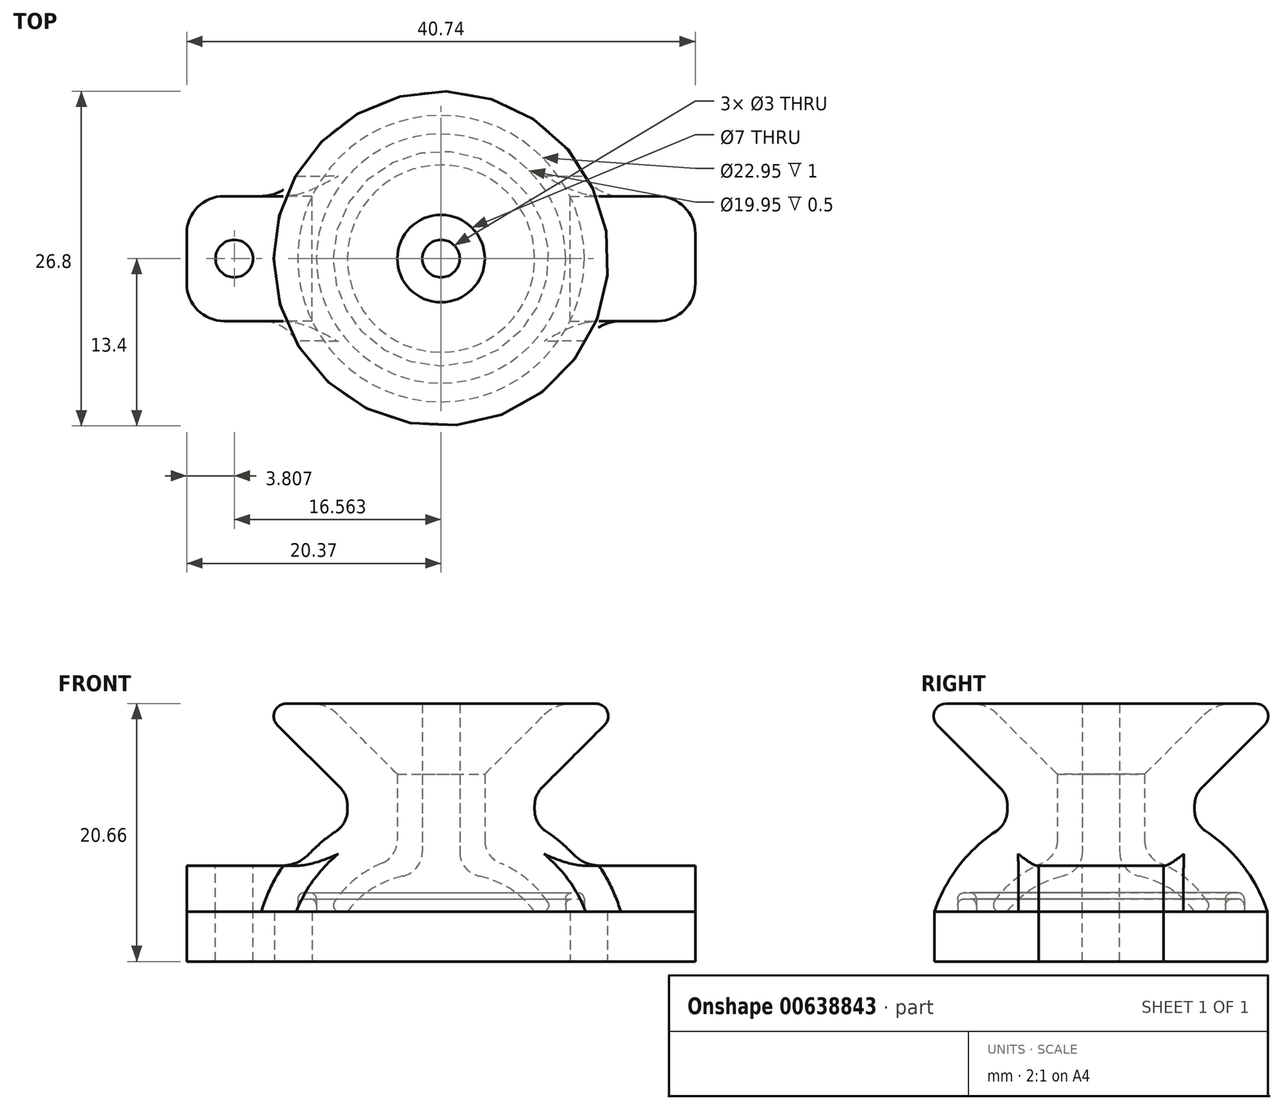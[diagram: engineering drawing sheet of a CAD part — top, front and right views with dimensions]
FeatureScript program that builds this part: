
annotation { "Feature Type Name" : "Feature", "Feature Type Description" : "" }
export const myFeature = defineFeature(function(context is Context, id is Id, definition is map)
    precondition{}
    {
        {
            var Q0;
            Q0=qCreatedBy(makeId("Front.planeOp"),FACE);
            var sketch = newSketch(context, id + "F0", { "sketchPlane" : qUnion([Q0])});
            skLineSegment(sketch, "E0", {"start": v(0, 0) * mm, "end": v(-1.5, 0) * mm, "construction": true});
            skLineSegment(sketch, "E1", {"start": v(-1.5, 1.79) * mm, "end": v(-1.5, 8) * mm});
            skPoint(sketch, "E2.endSnap0", {"position": v(-0.75, 0) * mm});
            skLineSegment(sketch, "E3", {"start": v(-1.5, 0) * mm, "end": v(-1.5, -3) * mm, "construction": true});
            skLineSegment(sketch, "E4", {"start": v(0, -3) * mm, "end": v(-7.5, -3) * mm, "construction": true});
            skLineSegment(sketch, "E5", {"start": v(-7.5, -3) * mm, "end": v(-8.12, -3) * mm});
            skArc(sketch, "E6", {"start": v(-3.08, -0.17) * mm, "mid": v(-5.55, -1.18) * mm, "end": v(-7.5, -3) * mm});
            skArc(sketch, "E7", {"start": v(-4.74, 0.87) * mm, "mid": v(-6.86, -0.4) * mm, "end": v(-8.53, -2.22) * mm});
            skLineSegment(sketch, "E8", {"start": v(-1.5, 8) * mm, "end": v(-3.5, 8) * mm});
            skLineSegment(sketch, "E9", {"start": v(-3.5, 8) * mm, "end": v(-3.5, 2.72) * mm});
            skLineSegment(sketch, "E10", {"start": v(0, -3) * mm, "end": v(0, 8.98) * mm, "construction": true});
            skPoint(sketch, "E11.visualSharp", {"position": v(-9, -3) * mm});
            skArc(sketch, "E11.filletArc", {"start": v(-8.53, -2.22) * mm, "mid": v(-8.56, -2.73) * mm, "end": v(-8.12, -3) * mm});
            skPoint(sketch, "E12.visualSharp", {"position": v(-1.5, 0) * mm});
            skArc(sketch, "E12.filletArc", {"start": v(-3.08, -0.17) * mm, "mid": v(-1.94, 0.53) * mm, "end": v(-1.5, 1.79) * mm});
            skPoint(sketch, "E13.visualSharp", {"position": v(-3.5, 1.27) * mm});
            skArc(sketch, "E13.filletArc", {"start": v(-4.74, 0.87) * mm, "mid": v(-3.84, 1.6) * mm, "end": v(-3.5, 2.72) * mm});
            skSolve(sketch);
        }
        {
            var Q0;
            Q0=makeQuery(id+"F0.imprint","IMPRINT",FACE,{"disambiguationData":[TD([[makeQuery(id+"F0.imprint","IMPRINT",EDGE,{"derivedFrom":sQuery(id+"F0.wireOp",EDGE,"E1")}),1.0]])]});
            var Q1;
            Q1=sQuery(id+"F0.wireOp",EDGE,"E10");
            revolve(context, id + "F1", {"entities" : qUnion([Q0]), "axis" : qUnion([Q1]), "revolveType" : RevolveType.FULL});
        }
        {
            var Q0;
            Q0=qCreatedBy(makeId("Front.planeOp"),FACE);
            var sketch = newSketch(context, id + "F2", { "sketchPlane" : qUnion([Q0])});
            skLineSegment(sketch, "E14.0", {"start": v(-3.5, 8) * mm, "end": v(-3.5, 2.72) * mm});
            skArc(sketch, "E14.1", {"start": v(-4.74, 0.87) * mm, "mid": v(-6.86, -0.4) * mm, "end": v(-8.53, -2.22) * mm});
            skArc(sketch, "E15.0", {"start": v(-8.4, 3.44) * mm, "mid": v(-11.4, 0.63) * mm, "end": v(-13.34, -3) * mm});
            skLineSegment(sketch, "E15.1", {"start": v(-7.5, 5.51) * mm, "end": v(-7.5, 5.1) * mm});
            skLineSegment(sketch, "E16.0", {"start": v(-1.5, 1.79) * mm, "end": v(-1.5, 8) * mm});
            skArc(sketch, "E16.1", {"start": v(-3.08, -0.17) * mm, "mid": v(-5.55, -1.18) * mm, "end": v(-7.5, -3) * mm});
            skLineSegment(sketch, "E16.2", {"start": v(-7.5, -3) * mm, "end": v(-8.12, -3) * mm});
            skArc(sketch, "E17.0", {"start": v(-4.74, 0.87) * mm, "mid": v(-3.84, 1.6) * mm, "end": v(-3.5, 2.72) * mm});
            skArc(sketch, "E18.0", {"start": v(-3.08, -0.17) * mm, "mid": v(-1.94, 0.53) * mm, "end": v(-1.5, 1.79) * mm});
            skArc(sketch, "E19.0", {"start": v(-8.53, -2.22) * mm, "mid": v(-8.56, -2.73) * mm, "end": v(-8.12, -3) * mm});
            skLineSegment(sketch, "E20", {"start": v(-8.12, -3) * mm, "end": v(-13.34, -3) * mm});
            skLineSegment(sketch, "E21", {"start": v(-13.34, -3) * mm, "end": v(-13.34, -7) * mm});
            skLineSegment(sketch, "E22", {"start": v(-13.34, -7) * mm, "end": v(0, -7) * mm});
            skLineSegment(sketch, "E23", {"start": v(0, -7) * mm, "end": v(0, 8) * mm});
            skLineSegment(sketch, "E24", {"start": v(0, 8) * mm, "end": v(-1.5, 8) * mm});
            skLineSegment(sketch, "E25", {"start": v(-13.34, -3) * mm, "end": v(-13.34, 0.67) * mm, "construction": true});
            skLineSegment(sketch, "E26", {"start": v(-11.37, 0.67) * mm, "end": v(-23.37, 0.67) * mm});
            skLineSegment(sketch, "E27", {"start": v(-23.37, 0.67) * mm, "end": v(-23.37, -3) * mm});
            skLineSegment(sketch, "E28", {"start": v(-23.37, -3) * mm, "end": v(-13.34, -3) * mm});
            skLineSegment(sketch, "E29", {"start": v(-13.34, -7) * mm, "end": v(-23.37, -7) * mm});
            skLineSegment(sketch, "E30", {"start": v(-23.37, -7) * mm, "end": v(-23.37, -3) * mm});
            skLineSegment(sketch, "E31", {"start": v(-3.5, 8) * mm, "end": v(-9.16, 13.66) * mm});
            skLineSegment(sketch, "E32", {"start": v(-9.16, 13.66) * mm, "end": v(-14.81, 13.66) * mm});
            skLineSegment(sketch, "E33.trimOffspring", {"start": v(-8.09, 6.93) * mm, "end": v(-14.81, 13.66) * mm});
            skPoint(sketch, "E34.visualSharp", {"position": v(-7.5, 6.34) * mm});
            skArc(sketch, "E34.filletArc", {"start": v(-7.5, 5.51) * mm, "mid": v(-7.65, 6.28) * mm, "end": v(-8.09, 6.93) * mm});
            skPoint(sketch, "E35.visualSharp", {"position": v(-7.5, 3.98) * mm});
            skArc(sketch, "E35.filletArc", {"start": v(-8.4, 3.44) * mm, "mid": v(-7.74, 4.16) * mm, "end": v(-7.5, 5.1) * mm});
            skLineSegment(sketch, "E36", {"start": v(0, 8) * mm, "end": v(0, 13.66) * mm});
            skLineSegment(sketch, "E37", {"start": v(0, 13.66) * mm, "end": v(-1.5, 13.66) * mm});
            skLineSegment(sketch, "E38", {"start": v(-1.5, 13.66) * mm, "end": v(-1.5, 8) * mm});
            skSolve(sketch);
        }
        {
            var Q0;
            Q0=makeQuery(id+"F2.imprint","IMPRINT",FACE,{"disambiguationData":[TD([[makeQuery(id+"F2.imprint","IMPRINT",EDGE,{"derivedFrom":sQuery(id+"F2.wireOp",EDGE,"E14.0")}),-1.0]])]});
            var Q1;
            Q1=sQuery(id+"F0.wireOp",EDGE,"E10");
            revolve(context, id + "F3", {"entities" : qUnion([Q0]), "axis" : qUnion([Q1]), "revolveType" : RevolveType.FULL});
        }
        {
            var Q0;
            Q0=makeQuery(id+"F2.imprint","IMPRINT",FACE,{"disambiguationData":[TD([[makeQuery(id+"F2.imprint","IMPRINT",EDGE,{"derivedFrom":sQuery(id+"F2.wireOp",EDGE,"E16.0")}),-1.0]])]});
            var Q1;
            Q1=makeQuery(id+"F2.imprint","IMPRINT",FACE,{"disambiguationData":[TD([[makeQuery(id+"F2.imprint","IMPRINT",EDGE,{"derivedFrom":sQuery(id+"F2.wireOp",EDGE,"E24")}),-1.0]])]});
            var Q2;
            Q2=sQuery(id+"F0.wireOp",EDGE,"E10");
            revolve(context, id + "F4", {"entities" : qUnion([Q0, Q1]), "axis" : qUnion([Q2]), "revolveType" : RevolveType.FULL});
        }
        {
            var Q0;
            {var subQ2=sQuery(id+"F2.wireOp",EDGE,"E26");Q0=makeQuery(id+"F2.imprint","IMPRINT",FACE,{"disambiguationData":[TD([[makeQuery(id+"F2.imprint","IMPRINT",EDGE,{"derivedFrom":subQ2}),1.0]])]});}
            extrude(context, id + "F5", {"entities" : qUnion([Q0]), "operationType" : NewBodyOperationType.ADD, "endBound" : BoundingType.SYMMETRIC, "depth" : 10 * mm, "offsetDistance" : 25 * mm});
        }
        {
            var Q0;
            Q0=makeQuery(id+"F2.imprint","IMPRINT",FACE,{"disambiguationData":[TD([[makeQuery(id+"F2.imprint","IMPRINT",EDGE,{"derivedFrom":sQuery(id+"F2.wireOp",EDGE,"E21")}),-1.0]])]});
            extrude(context, id + "F6", {"entities" : qUnion([Q0]), "endBound" : BoundingType.SYMMETRIC, "depth" : 10 * mm, "offsetDistance" : 25 * mm});
        }
        {
            var Q0;
            Q0=makeQuery(id+"F5.opExtrude","SWEPT_BODY",BODY,{"disambiguationData":[OSD([sQuery(id+"F2.wireOp",EDGE,"E15.0"),sQuery(id+"F2.wireOp",EDGE,"E26"),sQuery(id+"F2.wireOp",EDGE,"E27"),sQuery(id+"F2.wireOp",EDGE,"E28")])]});
            var Q1;
            Q1=makeQuery(id+"F6.opExtrude","SWEPT_BODY",BODY,{"disambiguationData":[OSD([sQuery(id+"F2.wireOp",EDGE,"E21"),sQuery(id+"F2.wireOp",EDGE,"E28"),sQuery(id+"F2.wireOp",EDGE,"E29"),sQuery(id+"F2.wireOp",EDGE,"E30")])]});
            transform(context, id + "F7", {"entities" : qUnion([Q0, Q1]), "transformType" : TransformType.TRANSLATION_3D, "dx" : 3 * mm, "dy" : 0 * mm, "dz" : 0 * mm, "makeCopy" : false});
        }
        {
            var Q0;
            Q0=makeQuery(id+"F5.opExtrude","SWEPT_BODY",BODY,{"disambiguationData":[OSD([sQuery(id+"F2.wireOp",EDGE,"E15.0"),sQuery(id+"F2.wireOp",EDGE,"E26"),sQuery(id+"F2.wireOp",EDGE,"E27"),sQuery(id+"F2.wireOp",EDGE,"E28")])]});
            var Q1;
            Q1=makeQuery(id+"F6.opExtrude","SWEPT_BODY",BODY,{"disambiguationData":[OSD([sQuery(id+"F2.wireOp",EDGE,"E21"),sQuery(id+"F2.wireOp",EDGE,"E28"),sQuery(id+"F2.wireOp",EDGE,"E29"),sQuery(id+"F2.wireOp",EDGE,"E30")])]});
            var Q2;
            Q2=qCreatedBy(makeId("Right.planeOp"),FACE);
            mirror(context, id + "F8", {"entities" : qUnion([Q0, Q1]), "mirrorPlane" : qUnion([Q2])});
        }
        {
            var Q0;
            Q0=makeQuery(id+"F5.opExtrude","SWEPT_BODY",BODY,{"disambiguationData":[OSD([sQuery(id+"F2.wireOp",EDGE,"E15.0"),sQuery(id+"F2.wireOp",EDGE,"E26"),sQuery(id+"F2.wireOp",EDGE,"E27"),sQuery(id+"F2.wireOp",EDGE,"E28")])]});
            var Q1;
            Q1=makeQuery(id+"F8.opPattern","COPY",BODY,{"derivedFrom":makeQuery(id+"F5.opExtrude","SWEPT_BODY",BODY,{"disambiguationData":[OSD([sQuery(id+"F2.wireOp",EDGE,"E15.0"),sQuery(id+"F2.wireOp",EDGE,"E26"),sQuery(id+"F2.wireOp",EDGE,"E27"),sQuery(id+"F2.wireOp",EDGE,"E28")])]}),"instanceName":"1"});
            var Q2;
            Q2=makeQuery(id+"F3.opRevolve","SWEPT_BODY",BODY,{"disambiguationData":[OSD([sQuery(id+"F2.wireOp",EDGE,"E14.0"),sQuery(id+"F2.wireOp",EDGE,"E14.1"),sQuery(id+"F2.wireOp",EDGE,"E15.0"),sQuery(id+"F2.wireOp",EDGE,"E15.1"),sQuery(id+"F2.wireOp",EDGE,"E17.0"),sQuery(id+"F2.wireOp",EDGE,"E19.0"),sQuery(id+"F2.wireOp",EDGE,"E20"),sQuery(id+"F2.wireOp",EDGE,"E31"),sQuery(id+"F2.wireOp",EDGE,"E32"),sQuery(id+"F2.wireOp",EDGE,"E33.trimOffspring"),sQuery(id+"F2.wireOp",EDGE,"E34.filletArc"),sQuery(id+"F2.wireOp",EDGE,"E35.filletArc")])]});
            booleanBodies(context, id + "F9", {"operationType" : BooleanOperationType.UNION, "tools" : qUnion([Q0, Q1, Q2])});
        }
        {
            var Q0;
            Q0=makeQuery(id+"F6.opExtrude","SWEPT_BODY",BODY,{"disambiguationData":[OSD([sQuery(id+"F2.wireOp",EDGE,"E21"),sQuery(id+"F2.wireOp",EDGE,"E28"),sQuery(id+"F2.wireOp",EDGE,"E29"),sQuery(id+"F2.wireOp",EDGE,"E30")])]});
            var Q1;
            Q1=makeQuery(id+"F4.opRevolve","SWEPT_BODY",BODY,{"disambiguationData":[OSD([sQuery(id+"F2.wireOp",EDGE,"E16.0"),sQuery(id+"F2.wireOp",EDGE,"E16.1"),sQuery(id+"F2.wireOp",EDGE,"E16.2"),sQuery(id+"F2.wireOp",EDGE,"E18.0"),sQuery(id+"F2.wireOp",EDGE,"E20"),sQuery(id+"F2.wireOp",EDGE,"E21"),sQuery(id+"F2.wireOp",EDGE,"E22"),sQuery(id+"F2.wireOp",EDGE,"E23"),sQuery(id+"F2.wireOp",EDGE,"E36"),sQuery(id+"F2.wireOp",EDGE,"E37"),sQuery(id+"F2.wireOp",EDGE,"E38")])]});
            var Q2;
            Q2=makeQuery(id+"F8.opPattern","COPY",BODY,{"derivedFrom":makeQuery(id+"F6.opExtrude","SWEPT_BODY",BODY,{"disambiguationData":[OSD([sQuery(id+"F2.wireOp",EDGE,"E21"),sQuery(id+"F2.wireOp",EDGE,"E28"),sQuery(id+"F2.wireOp",EDGE,"E29"),sQuery(id+"F2.wireOp",EDGE,"E30")])]}),"instanceName":"1"});
            booleanBodies(context, id + "F10", {"operationType" : BooleanOperationType.UNION, "tools" : qUnion([Q0, Q1, Q2])});
        }
        {
            var Q0;
            Q0=makeQuery(id+"F8.opPattern","COPY",EDGE,{"derivedFrom":makeQuery(id+"F5.opExtrude","CAP_EDGE",EDGE,{"disambiguationData":[OSD([sQuery(id+"F2.wireOp",EDGE,"E27")])],"isStart":false}),"instanceName":"1"});
            var Q1;
            Q1=makeQuery(id+"F8.opPattern","COPY",EDGE,{"derivedFrom":makeQuery(id+"F5.opExtrude","CAP_EDGE",EDGE,{"disambiguationData":[OSD([sQuery(id+"F2.wireOp",EDGE,"E27")])],"isStart":true}),"instanceName":"1"});
            var Q2;
            Q2=makeQuery(id+"F8.opPattern","COPY",EDGE,{"derivedFrom":makeQuery(id+"F6.opExtrude","CAP_EDGE",EDGE,{"disambiguationData":[OSD([sQuery(id+"F2.wireOp",EDGE,"E30")])],"isStart":true}),"instanceName":"1"});
            var Q3;
            Q3=makeQuery(id+"F8.opPattern","COPY",EDGE,{"derivedFrom":makeQuery(id+"F6.opExtrude","CAP_EDGE",EDGE,{"disambiguationData":[OSD([sQuery(id+"F2.wireOp",EDGE,"E30")])],"isStart":false}),"instanceName":"1"});
            var Q4;
            {var subQ0=sQuery(id+"F2.wireOp",EDGE,"E21");Q4=makeQuery(id+"F10.opBoolean","INTERSECT",EDGE,{"derivedFrom":[makeQuery(id+"F4.opRevolve","SWEPT_FACE",FACE,{"disambiguationData":[OSD([subQ0])]}),makeQuery(id+"F8.opPattern","COPY",FACE,{"derivedFrom":makeQuery(id+"F6.opExtrude","CAP_FACE",FACE,{"disambiguationData":[OSD([subQ0,sQuery(id+"F2.wireOp",EDGE,"E28"),sQuery(id+"F2.wireOp",EDGE,"E29"),sQuery(id+"F2.wireOp",EDGE,"E30")])],"isStart":false}),"instanceName":"1"})]});}
            var Q5;
            {var subQ0=sQuery(id+"F2.wireOp",EDGE,"E21");Q5=makeQuery(id+"F10.opBoolean","INTERSECT",EDGE,{"derivedFrom":[makeQuery(id+"F4.opRevolve","SWEPT_FACE",FACE,{"disambiguationData":[OSD([subQ0])]}),makeQuery(id+"F8.opPattern","COPY",FACE,{"derivedFrom":makeQuery(id+"F6.opExtrude","CAP_FACE",FACE,{"disambiguationData":[OSD([subQ0,sQuery(id+"F2.wireOp",EDGE,"E28"),sQuery(id+"F2.wireOp",EDGE,"E29"),sQuery(id+"F2.wireOp",EDGE,"E30")])],"isStart":true}),"instanceName":"1"})]});}
            var Q6;
            {var subQ0=sQuery(id+"F2.wireOp",EDGE,"E21");Q6=makeQuery(id+"F10.opBoolean","INTERSECT",EDGE,{"derivedFrom":[makeQuery(id+"F4.opRevolve","SWEPT_FACE",FACE,{"disambiguationData":[OSD([subQ0])]}),makeQuery(id+"F6.opExtrude","CAP_FACE",FACE,{"disambiguationData":[OSD([subQ0,sQuery(id+"F2.wireOp",EDGE,"E28"),sQuery(id+"F2.wireOp",EDGE,"E29"),sQuery(id+"F2.wireOp",EDGE,"E30")])],"isStart":false})]});}
            var Q7;
            Q7=makeQuery(id+"F6.opExtrude","CAP_EDGE",EDGE,{"disambiguationData":[OSD([sQuery(id+"F2.wireOp",EDGE,"E30")])],"isStart":false});
            var Q8;
            Q8=makeQuery(id+"F5.opExtrude","CAP_EDGE",EDGE,{"disambiguationData":[OSD([sQuery(id+"F2.wireOp",EDGE,"E27")])],"isStart":false});
            var Q9;
            Q9=makeQuery(id+"F5.opExtrude","CAP_EDGE",EDGE,{"disambiguationData":[OSD([sQuery(id+"F2.wireOp",EDGE,"E27")])],"isStart":true});
            var Q10;
            Q10=makeQuery(id+"F6.opExtrude","CAP_EDGE",EDGE,{"disambiguationData":[OSD([sQuery(id+"F2.wireOp",EDGE,"E30")])],"isStart":true});
            var Q11;
            {var subQ0=sQuery(id+"F2.wireOp",EDGE,"E21");Q11=makeQuery(id+"F10.opBoolean","INTERSECT",EDGE,{"derivedFrom":[makeQuery(id+"F4.opRevolve","SWEPT_FACE",FACE,{"disambiguationData":[OSD([subQ0])]}),makeQuery(id+"F6.opExtrude","CAP_FACE",FACE,{"disambiguationData":[OSD([subQ0,sQuery(id+"F2.wireOp",EDGE,"E28"),sQuery(id+"F2.wireOp",EDGE,"E29"),sQuery(id+"F2.wireOp",EDGE,"E30")])],"isStart":true})]});}
            var Q12;
            {var subQ0=sQuery(id+"F2.wireOp",EDGE,"E15.0");Q12=makeQuery(id+"F9.opBoolean","INTERSECT",EDGE,{"derivedFrom":[makeQuery(id+"F3.opRevolve","SWEPT_FACE",FACE,{"disambiguationData":[OSD([subQ0])]}),makeQuery(id+"F5.opExtrude","CAP_FACE",FACE,{"disambiguationData":[OSD([subQ0,sQuery(id+"F2.wireOp",EDGE,"E26"),sQuery(id+"F2.wireOp",EDGE,"E27"),sQuery(id+"F2.wireOp",EDGE,"E28")])],"isStart":true})]});}
            var Q13;
            {var subQ0=sQuery(id+"F2.wireOp",EDGE,"E15.0");Q13=makeQuery(id+"F9.opBoolean","INTERSECT",EDGE,{"derivedFrom":[makeQuery(id+"F3.opRevolve","SWEPT_FACE",FACE,{"disambiguationData":[OSD([subQ0])]}),makeQuery(id+"F5.opExtrude","CAP_FACE",FACE,{"disambiguationData":[OSD([subQ0,sQuery(id+"F2.wireOp",EDGE,"E26"),sQuery(id+"F2.wireOp",EDGE,"E27"),sQuery(id+"F2.wireOp",EDGE,"E28")])],"isStart":false})]});}
            var Q14;
            {var subQ0=sQuery(id+"F2.wireOp",EDGE,"E15.0");Q14=makeQuery(id+"F9.opBoolean","INTERSECT",EDGE,{"derivedFrom":[makeQuery(id+"F3.opRevolve","SWEPT_FACE",FACE,{"disambiguationData":[OSD([subQ0])]}),makeQuery(id+"F8.opPattern","COPY",FACE,{"derivedFrom":makeQuery(id+"F5.opExtrude","CAP_FACE",FACE,{"disambiguationData":[OSD([subQ0,sQuery(id+"F2.wireOp",EDGE,"E26"),sQuery(id+"F2.wireOp",EDGE,"E27"),sQuery(id+"F2.wireOp",EDGE,"E28")])],"isStart":false}),"instanceName":"1"})]});}
            var Q15;
            {var subQ0=sQuery(id+"F2.wireOp",EDGE,"E15.0");Q15=makeQuery(id+"F9.opBoolean","INTERSECT",EDGE,{"derivedFrom":[makeQuery(id+"F3.opRevolve","SWEPT_FACE",FACE,{"disambiguationData":[OSD([subQ0])]}),makeQuery(id+"F8.opPattern","COPY",FACE,{"derivedFrom":makeQuery(id+"F5.opExtrude","CAP_FACE",FACE,{"disambiguationData":[OSD([subQ0,sQuery(id+"F2.wireOp",EDGE,"E26"),sQuery(id+"F2.wireOp",EDGE,"E27"),sQuery(id+"F2.wireOp",EDGE,"E28")])],"isStart":true}),"instanceName":"1"})]});}
            var Q16;
            Q16=makeQuery(id+"F9.opBoolean","INTERSECT",EDGE,{"derivedFrom":[makeQuery(id+"F3.opRevolve","SWEPT_FACE",FACE,{"disambiguationData":[OSD([sQuery(id+"F2.wireOp",EDGE,"E15.0")])]}),makeQuery(id+"F8.opPattern","COPY",FACE,{"derivedFrom":makeQuery(id+"F5.opExtrude","SWEPT_FACE",FACE,{"disambiguationData":[OSD([sQuery(id+"F2.wireOp",EDGE,"E26")])]}),"instanceName":"1"})]});
            var Q17;
            Q17=makeQuery(id+"F9.opBoolean","INTERSECT",EDGE,{"derivedFrom":[makeQuery(id+"F3.opRevolve","SWEPT_FACE",FACE,{"disambiguationData":[OSD([sQuery(id+"F2.wireOp",EDGE,"E15.0")])]}),makeQuery(id+"F5.opExtrude","SWEPT_FACE",FACE,{"disambiguationData":[OSD([sQuery(id+"F2.wireOp",EDGE,"E26")])]})]});
            var Q18;
            Q18=makeQuery(id+"F3.opRevolve","SWEPT_EDGE",EDGE,{"disambiguationData":[OSD([sQuery(id+"F2.wireOp",EDGE,"E31"),sQuery(id+"F2.wireOp",EDGE,"E32")])]});
            fillet(context, id + "F11", {"entities" : qUnion([Q0, Q1, Q2, Q3, Q4, Q5, Q6, Q7, Q8, Q9, Q10, Q11, Q12, Q13, Q14, Q15, Q16, Q17, Q18]), "radius" : 3 * mm, "tangentPropagation" : true, "allowEdgeOverflow" : false});
        }
        {
            var Q0;
            Q0=makeQuery(id+"F3.opRevolve","SWEPT_EDGE",EDGE,{"disambiguationData":[OSD([sQuery(id+"F2.wireOp",EDGE,"E32"),sQuery(id+"F2.wireOp",EDGE,"E33.trimOffspring")])]});
            fillet(context, id + "F12", {"entities" : qUnion([Q0]), "radius" : 1 * mm, "tangentPropagation" : true, "allowEdgeOverflow" : false});
        }
        {
            var Q0;
            {var subQ0=makeQuery(id+"F5.opExtrude","SWEPT_FACE",FACE,{"disambiguationData":[OSD([sQuery(id+"F2.wireOp",EDGE,"E28")])]});Q0=makeQuery(id+"F9.opBoolean","MERGE",FACE,{"derivedFrom":[makeQuery(id+"F3.opRevolve","SWEPT_FACE",FACE,{"disambiguationData":[OSD([sQuery(id+"F2.wireOp",EDGE,"E20")])]}),subQ0,makeQuery(id+"F8.opPattern","COPY",FACE,{"derivedFrom":subQ0,"instanceName":"1"})]});}
            var sketch = newSketch(context, id + "F13", { "sketchPlane" : qUnion([Q0])});
            skLineSegment(sketch, "E39", {"start": v(0, 13.34) * mm, "end": v(0, 8.12) * mm, "construction": true});
            skPoint(sketch, "E40", {"position": v(0, 10.73) * mm});
            skPoint(sketch, "E41", {"position": v(0, 11.48) * mm});
            skPoint(sketch, "E42", {"position": v(0, 9.98) * mm});
            skCircle(sketch, "E43", {"center": v(0, 0) * mm, "radius": 9.98 * mm});
            skCircle(sketch, "E44", {"center": v(0, 0) * mm, "radius": 11.48 * mm});
            skSolve(sketch);
        }
        {
            var Q0;
            Q0=makeQuery(id+"F13.imprint","IMPRINT",FACE,{"disambiguationData":[TD([[makeQuery(id+"F13.imprint","IMPRINT",EDGE,{"derivedFrom":sQuery(id+"F13.wireOp",EDGE,"E43")}),-1.0]])]});
            extrude(context, id + "F14", {"entities" : qUnion([Q0]), "oppositeDirection" : true, "depth" : 1.5 * mm, "offsetDistance" : 25 * mm});
        }
        {
            var Q0;
            Q0=makeQuery(id+"F14.opExtrude","CAP_EDGE",EDGE,{"disambiguationData":[OSD([sQuery(id+"F13.wireOp",EDGE,"E44")])],"isStart":false});
            var Q1;
            Q1=makeQuery(id+"F14.opExtrude","CAP_EDGE",EDGE,{"disambiguationData":[OSD([sQuery(id+"F13.wireOp",EDGE,"E43")])],"isStart":false});
            fillet(context, id + "F15", {"entities" : qUnion([Q0, Q1]), "radius" : 0.5 * mm, "tangentPropagation" : true, "allowEdgeOverflow" : false});
        }
        {
            var Q0;
            Q0=makeQuery(id+"F14.opExtrude","SWEPT_BODY",BODY,{"disambiguationData":[OSD([sQuery(id+"F13.wireOp",EDGE,"E43"),sQuery(id+"F13.wireOp",EDGE,"E44")])]});
            var Q1;
            Q1=makeQuery(id+"F5.opExtrude","SWEPT_BODY",BODY,{"disambiguationData":[OSD([sQuery(id+"F2.wireOp",EDGE,"E15.0"),sQuery(id+"F2.wireOp",EDGE,"E26"),sQuery(id+"F2.wireOp",EDGE,"E27"),sQuery(id+"F2.wireOp",EDGE,"E28")])]});
            booleanBodies(context, id + "F16", {"operationType" : BooleanOperationType.SUBTRACTION, "tools" : qUnion([Q0]), "targets" : qUnion([Q1])});
        }
        {
            var Q0;
            Q0=makeQuery(id+"F13.imprint","IMPRINT",FACE,{"disambiguationData":[TD([[makeQuery(id+"F13.imprint","IMPRINT",EDGE,{"derivedFrom":sQuery(id+"F13.wireOp",EDGE,"E43")}),-1.0]])]});
            extrude(context, id + "F17", {"entities" : qUnion([Q0]), "oppositeDirection" : true, "depth" : 1 * mm, "offsetDistance" : 25 * mm});
        }
        {
            var Q0;
            Q0=makeQuery(id+"F17.opExtrude","CAP_EDGE",EDGE,{"disambiguationData":[OSD([sQuery(id+"F13.wireOp",EDGE,"E44")])],"isStart":false});
            var Q1;
            Q1=makeQuery(id+"F17.opExtrude","CAP_EDGE",EDGE,{"disambiguationData":[OSD([sQuery(id+"F13.wireOp",EDGE,"E43")])],"isStart":false});
            fillet(context, id + "F18", {"entities" : qUnion([Q0, Q1]), "radius" : 0.5 * mm, "tangentPropagation" : true, "allowEdgeOverflow" : false});
        }
        {
            var Q0;
            Q0=makeQuery(id+"F5.opExtrude","SWEPT_FACE",FACE,{"disambiguationData":[OSD([sQuery(id+"F2.wireOp",EDGE,"E26")])]});
            var sketch = newSketch(context, id + "F19", { "sketchPlane" : qUnion([Q0])});
            skLineSegment(sketch, "E45", {"start": v(-12.75, 0) * mm, "end": v(-20.37, 0) * mm, "construction": true});
            skCircle(sketch, "E46", {"center": v(-16.56, 0) * mm, "radius": 1.5 * mm});
            skLineSegment(sketch, "E47", {"start": v(0, 0) * mm, "end": v(0, 16.55) * mm, "construction": true});
            skCircle(sketch, "E48.MirrorC", {"center": v(16.56, 0) * mm, "radius": 1.5 * mm});
            skSolve(sketch);
        }
        {
            var Q0;
            Q0=makeQuery(id+"F19.imprint","IMPRINT",FACE,{"disambiguationData":[TD([[makeQuery(id+"F19.imprint","IMPRINT",EDGE,{"derivedFrom":sQuery(id+"F19.wireOp",EDGE,"E46")}),1.0]])]});
            var Q1;
            Q1=makeQuery(id+"F19.imprint","IMPRINT",FACE,{"disambiguationData":[TD([[makeQuery(id+"F19.imprint","IMPRINT",EDGE,{"derivedFrom":sQuery(id+"F19.wireOp",EDGE,"E48.MirrorC")}),-1.0]])]});
            extrude(context, id + "F20", {"entities" : qUnion([Q0, Q1]), "operationType" : NewBodyOperationType.REMOVE, "oppositeDirection" : true, "depth" : 25 * mm, "offsetDistance" : 25 * mm});
        }
    });
